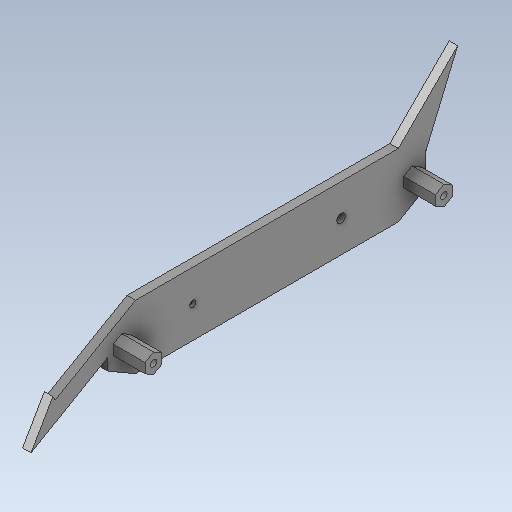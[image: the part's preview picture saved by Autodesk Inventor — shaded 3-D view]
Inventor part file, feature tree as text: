
AUTODESK INVENTOR PART (.ipt)
format: ipt  version: 2020 (Build 240168000, 168)  size: 175,616 bytes
history: native  units: in
note: dims shown in document units (in); Inventor stores cm internally (conversion verified against a paired STEP export)
features: other x3, extrude x2, sketch x2
ambient origin geometry x8: Origin, YZ Plane, XZ Plane, XY Plane, X Axis, Y Axis, Z Axis, Center Point
bodies: Solid1 (feature_tree)
feature tree (7):
  other  "HexWheelGuard.ipt"
  extrude  "Extrusion1"  TaperAngle=0.0deg  [1 undecoded]
  extrude  "Extrusion2"  Depth=0.5906in
  other  "Solid1::HexWheelGuard.ipt"
  other  "TaggingFeature1"
  sketch  "Sketch1"  dims[d0=0.3937in d6=0.0in d7=0.0in]
  sketch  "Sketch2"  dims[d9=0.315in d10=1.4843in d11=60.0deg d12=0.0787in d13=0.3937in d14=0.0in d20=0.3937in d21=0.5906in d22=1.1024in]
note: 1 required parameter value undecoded (feature->parameter linkage not recoverable at this tier; creation-order binding heuristic only, values carry confidence <= 0.55)
